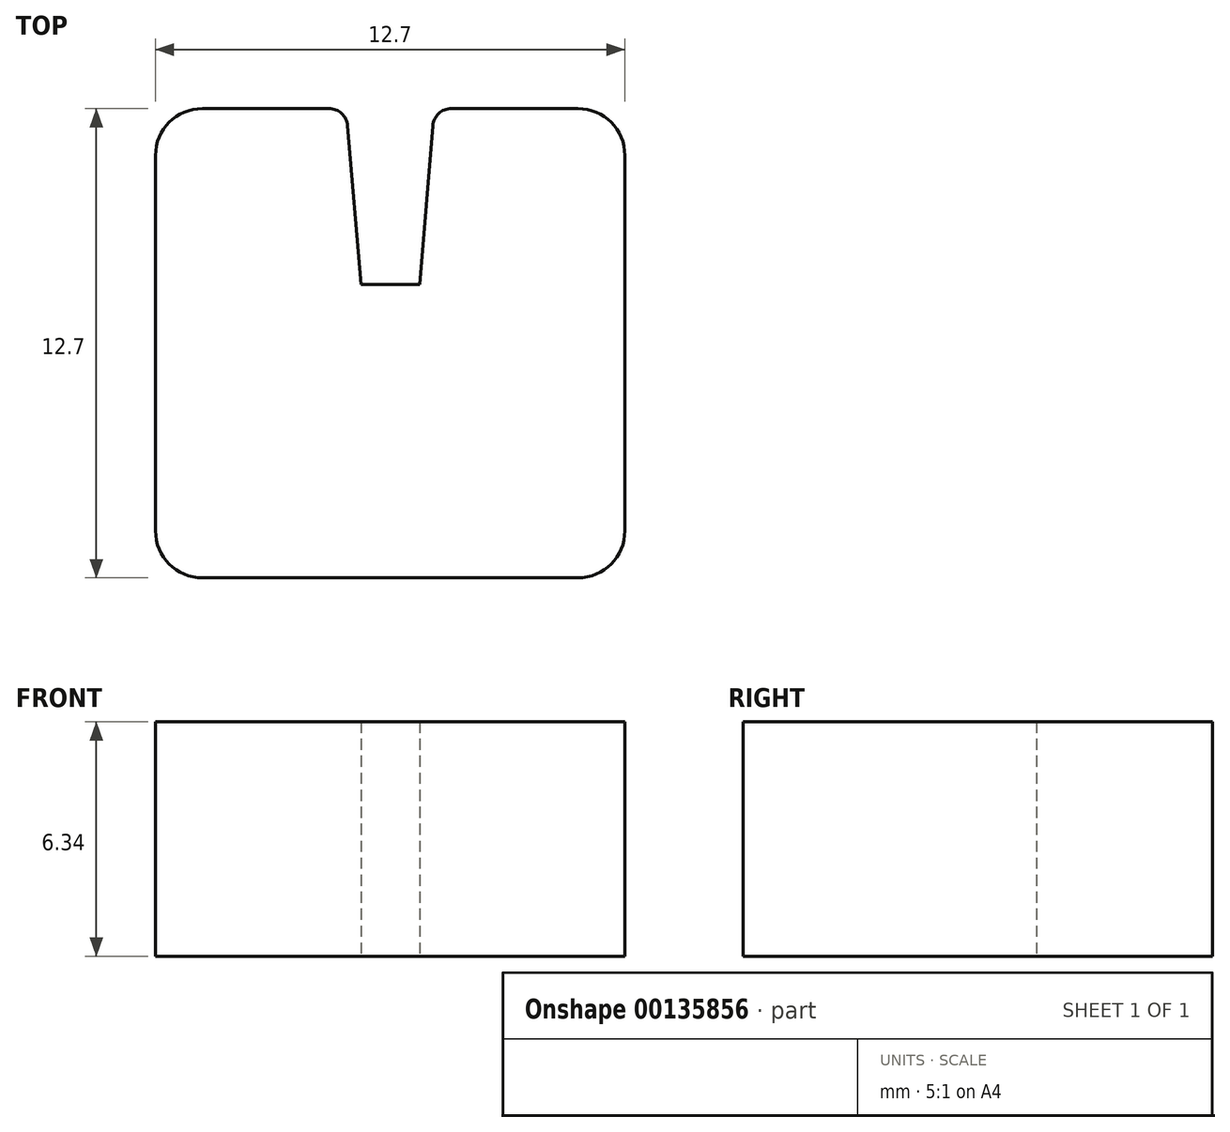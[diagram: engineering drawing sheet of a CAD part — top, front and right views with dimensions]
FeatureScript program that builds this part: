
annotation { "Feature Type Name" : "Feature", "Feature Type Description" : "" }
export const myFeature = defineFeature(function(context is Context, id is Id, definition is map)
    precondition{}
    {
        {
            var Q0;
            Q0=qCreatedBy(makeId("Top.planeOp"),FACE);
            var sketch = newSketch(context, id + "F0", { "sketchPlane" : qUnion([Q0])});
            skLineSegment(sketch, "E0", {"start": v(-6.35, 3.34) * mm, "end": v(6.35, 3.34) * mm});
            skLineSegment(sketch, "E1", {"start": v(6.35, 3.34) * mm, "end": v(6.35, 16.04) * mm});
            skLineSegment(sketch, "E2", {"start": v(6.35, 16.04) * mm, "end": v(1.2, 16.04) * mm});
            skLineSegment(sketch, "E3", {"start": v(1.2, 16.04) * mm, "end": v(0.8, 11.28) * mm});
            skLineSegment(sketch, "E4", {"start": v(0.8, 11.28) * mm, "end": v(-0.8, 11.28) * mm});
            skLineSegment(sketch, "E5", {"start": v(-0.8, 11.28) * mm, "end": v(-1.2, 16.04) * mm});
            skLineSegment(sketch, "E6", {"start": v(-1.2, 16.04) * mm, "end": v(-6.35, 16.04) * mm});
            skLineSegment(sketch, "E7", {"start": v(-6.35, 16.04) * mm, "end": v(-6.35, 3.34) * mm});
            skSolve(sketch);
        }
        {
            var Q0;
            Q0 = qSketchRegion(id + "F0", true);
            extrude(context, id + "F1", {"entities" : qUnion([Q0]), "endBound" : BoundingType.SYMMETRIC, "depth" : 6.35 * mm});
        }
        {
            var Q0;
            Q0=makeQuery(id+"F1.opExtrude","SWEPT_EDGE",EDGE,{"disambiguationData":[OSD([sQuery(id+"F0.wireOp",EDGE,"E0"),sQuery(id+"F0.wireOp",EDGE,"E7")])]});
            var Q1;
            Q1=makeQuery(id+"F1.opExtrude","SWEPT_EDGE",EDGE,{"disambiguationData":[OSD([sQuery(id+"F0.wireOp",EDGE,"E0"),sQuery(id+"F0.wireOp",EDGE,"E1")])]});
            var Q2;
            Q2=makeQuery(id+"F1.opExtrude","SWEPT_EDGE",EDGE,{"disambiguationData":[OSD([sQuery(id+"F0.wireOp",EDGE,"E1"),sQuery(id+"F0.wireOp",EDGE,"E2")])]});
            var Q3;
            Q3=makeQuery(id+"F1.opExtrude","SWEPT_EDGE",EDGE,{"disambiguationData":[OSD([sQuery(id+"F0.wireOp",EDGE,"E6"),sQuery(id+"F0.wireOp",EDGE,"E7")])]});
            fillet(context, id + "F2", {"entities" : qUnion([Q0, Q1, Q2, Q3]), "radius" : 1.27 * mm, "tangentPropagation" : true, "allowEdgeOverflow" : false});
        }
        {
            var Q0;
            Q0=makeQuery(id+"F1.opExtrude","SWEPT_EDGE",EDGE,{"disambiguationData":[OSD([sQuery(id+"F0.wireOp",EDGE,"E2"),sQuery(id+"F0.wireOp",EDGE,"E3")])]});
            var Q1;
            Q1=makeQuery(id+"F1.opExtrude","SWEPT_EDGE",EDGE,{"disambiguationData":[OSD([sQuery(id+"F0.wireOp",EDGE,"E5"),sQuery(id+"F0.wireOp",EDGE,"E6")])]});
            fillet(context, id + "F3", {"entities" : qUnion([Q0, Q1]), "radius" : 0.5 * mm, "tangentPropagation" : true, "allowEdgeOverflow" : false});
        }
    });
